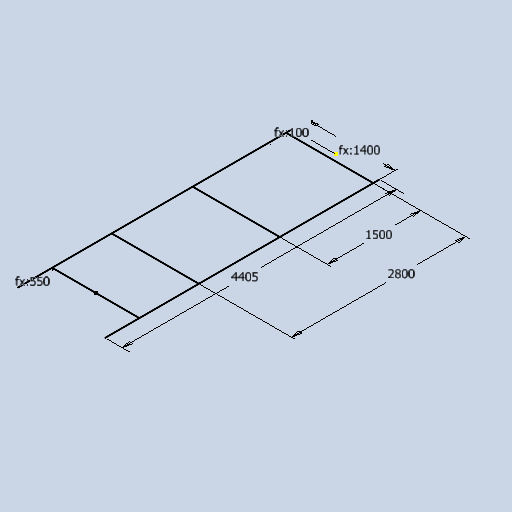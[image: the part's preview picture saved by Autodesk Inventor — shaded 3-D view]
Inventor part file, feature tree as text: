
AUTODESK INVENTOR PART (.ipt)
format: ipt  version: 2025 (Build 290162010, 162A)  size: 265,216 bytes
history: native  units: in
note: dims shown in document units (in); Inventor stores cm internally (conversion verified against a paired STEP export)
features: sketch x1
ambient origin geometry x8: Origin, YZ Plane, XZ Plane, XY Plane, X Axis, Y Axis, Z Axis, Center Point
feature tree (1):
  sketch  "Sketch3"  dims[d7=173.4252in d8=3.937in d9=21.6535in d10=55.1181in d11=59.0551in d12=110.2362in]
